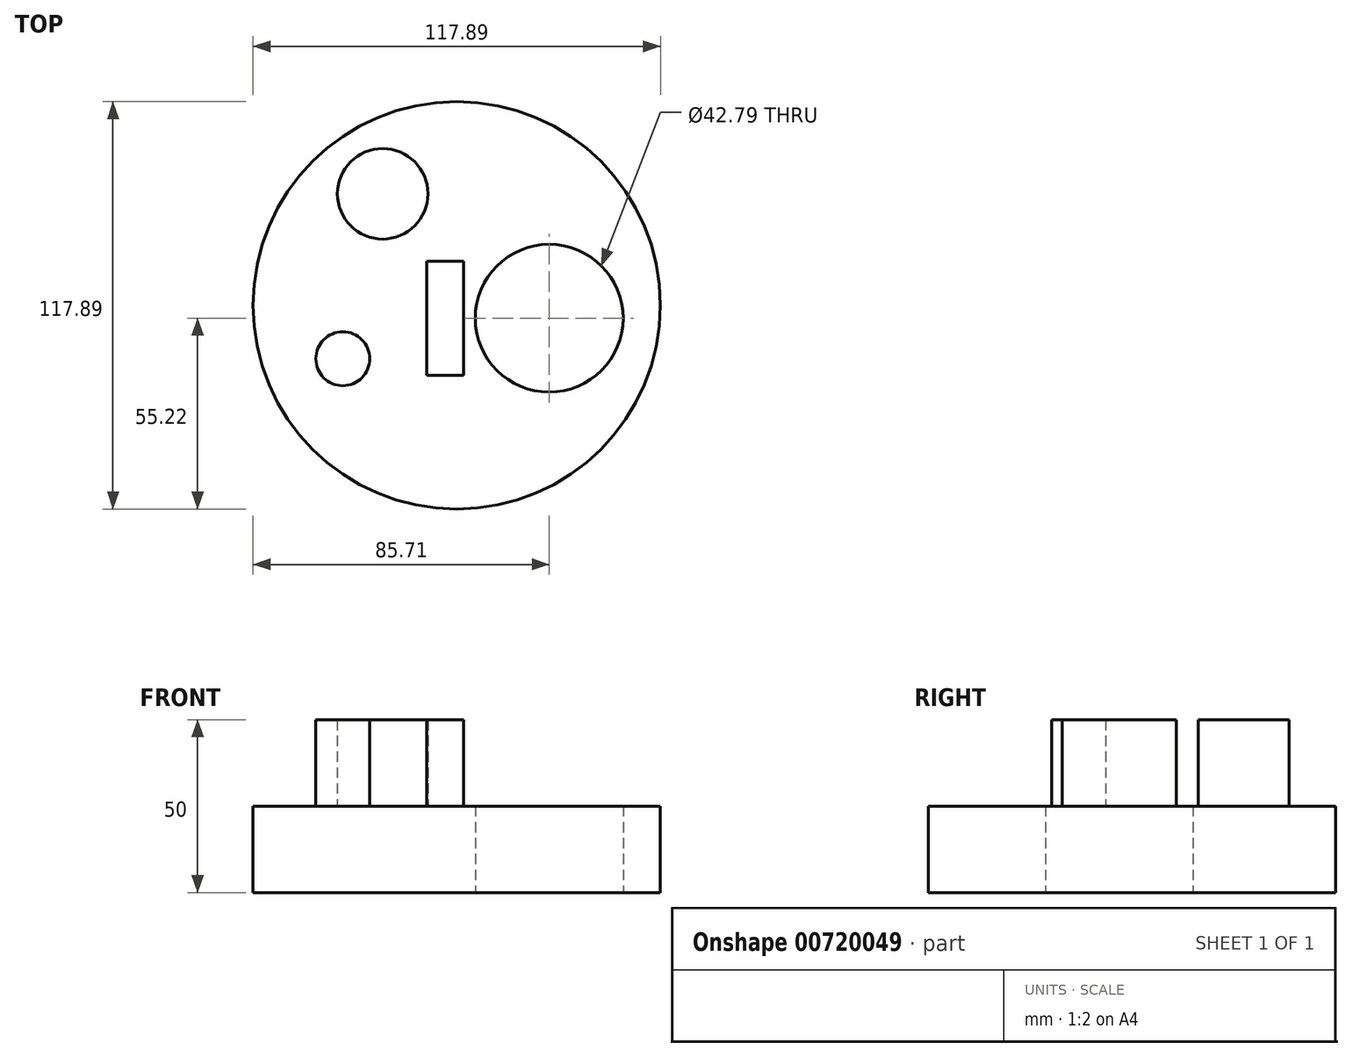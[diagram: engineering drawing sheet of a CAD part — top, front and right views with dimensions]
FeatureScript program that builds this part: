
annotation { "Feature Type Name" : "Feature", "Feature Type Description" : "" }
export const myFeature = defineFeature(function(context is Context, id is Id, definition is map)
    precondition{}
    {
        {
            var Q0;
            Q0=qCreatedBy(makeId("Top.planeOp"),FACE);
            var sketch = newSketch(context, id + "F0", { "sketchPlane" : qUnion([Q0])});
            skCircle(sketch, "E0", {"center": v(-7.24, 0) * mm, "radius": 21.4 * mm});
            skCircle(sketch, "E1", {"center": v(-34, 3.73) * mm, "radius": 58.94 * mm});
            skSolve(sketch);
        }
        {
            var Q0;
            Q0=makeQuery(id+"F0.imprint","IMPRINT",FACE,{"disambiguationData":[TD([[makeQuery(id+"F0.imprint","IMPRINT",EDGE,{"derivedFrom":sQuery(id+"F0.wireOp",EDGE,"E0")}),-1.0]])]});
            extrude(context, id + "F1", {"entities" : qUnion([Q0]), "depth" : 25 * mm, "offsetDistance" : 25 * mm});
        }
        {
            var Q0;
            Q0=makeQuery(id+"F1.opExtrude","CAP_FACE",FACE,{"disambiguationData":[OSD([sQuery(id+"F0.wireOp",EDGE,"E0"),sQuery(id+"F0.wireOp",EDGE,"E1")])],"isStart":false});
            var sketch = newSketch(context, id + "F2", { "sketchPlane" : qUnion([Q0])});
            skCircle(sketch, "E2", {"center": v(-66.98, -11.73) * mm, "radius": 7.8 * mm});
            skCircle(sketch, "E3", {"center": v(-55.42, 36) * mm, "radius": 13.1 * mm});
            skSolve(sketch);
        }
        {
            var Q0;
            Q0=makeQuery(id+"F2.imprint","IMPRINT",FACE,{"disambiguationData":[TD([[makeQuery(id+"F2.imprint","IMPRINT",EDGE,{"derivedFrom":sQuery(id+"F2.wireOp",EDGE,"E2")}),1.0]])]});
            var Q1;
            Q1=makeQuery(id+"F2.imprint","IMPRINT",FACE,{"disambiguationData":[TD([[makeQuery(id+"F2.imprint","IMPRINT",EDGE,{"derivedFrom":sQuery(id+"F2.wireOp",EDGE,"E3")}),1.0]])]});
            extrude(context, id + "F3", {"entities" : qUnion([Q0, Q1]), "operationType" : NewBodyOperationType.ADD, "depth" : 25 * mm, "offsetDistance" : 25 * mm});
        }
        {
            var Q0;
            Q0=makeQuery(id+"F2.imprint","IMPRINT",FACE,{"disambiguationData":[TD([[makeQuery(id+"F2.imprint","IMPRINT",EDGE,{"derivedFrom":sQuery(id+"F2.wireOp",EDGE,"E2")}),1.0]])]});
            extrude(context, id + "F4", {"entities" : qUnion([Q0]), "operationType" : NewBodyOperationType.ADD, "depth" : 25 * mm, "offsetDistance" : 25 * mm});
        }
        {
            var Q0;
            Q0=makeQuery(id+"F1.opExtrude","CAP_FACE",FACE,{"disambiguationData":[OSD([sQuery(id+"F0.wireOp",EDGE,"E0"),sQuery(id+"F0.wireOp",EDGE,"E1")])],"isStart":false});
            var sketch = newSketch(context, id + "F5", { "sketchPlane" : qUnion([Q0])});
            skLineSegment(sketch, "E4.bottom", {"start": v(-42.73, 16.48) * mm, "end": v(-32, 16.48) * mm});
            skLineSegment(sketch, "E4.top", {"start": v(-42.73, -16.48) * mm, "end": v(-32, -16.48) * mm});
            skLineSegment(sketch, "E4.left", {"start": v(-42.73, 16.48) * mm, "end": v(-42.73, -16.48) * mm});
            skLineSegment(sketch, "E4.right", {"start": v(-32, 16.48) * mm, "end": v(-32, -16.48) * mm});
            skPoint(sketch, "E4.middle", {"position": v(-37.36, 0) * mm});
            skSolve(sketch);
        }
        {
            var Q0;
            Q0 = qSketchRegion(id + "F5", true);
            extrude(context, id + "F6", {"entities" : qUnion([Q0]), "operationType" : NewBodyOperationType.ADD, "depth" : 25 * mm, "offsetDistance" : 25 * mm});
        }
    });
